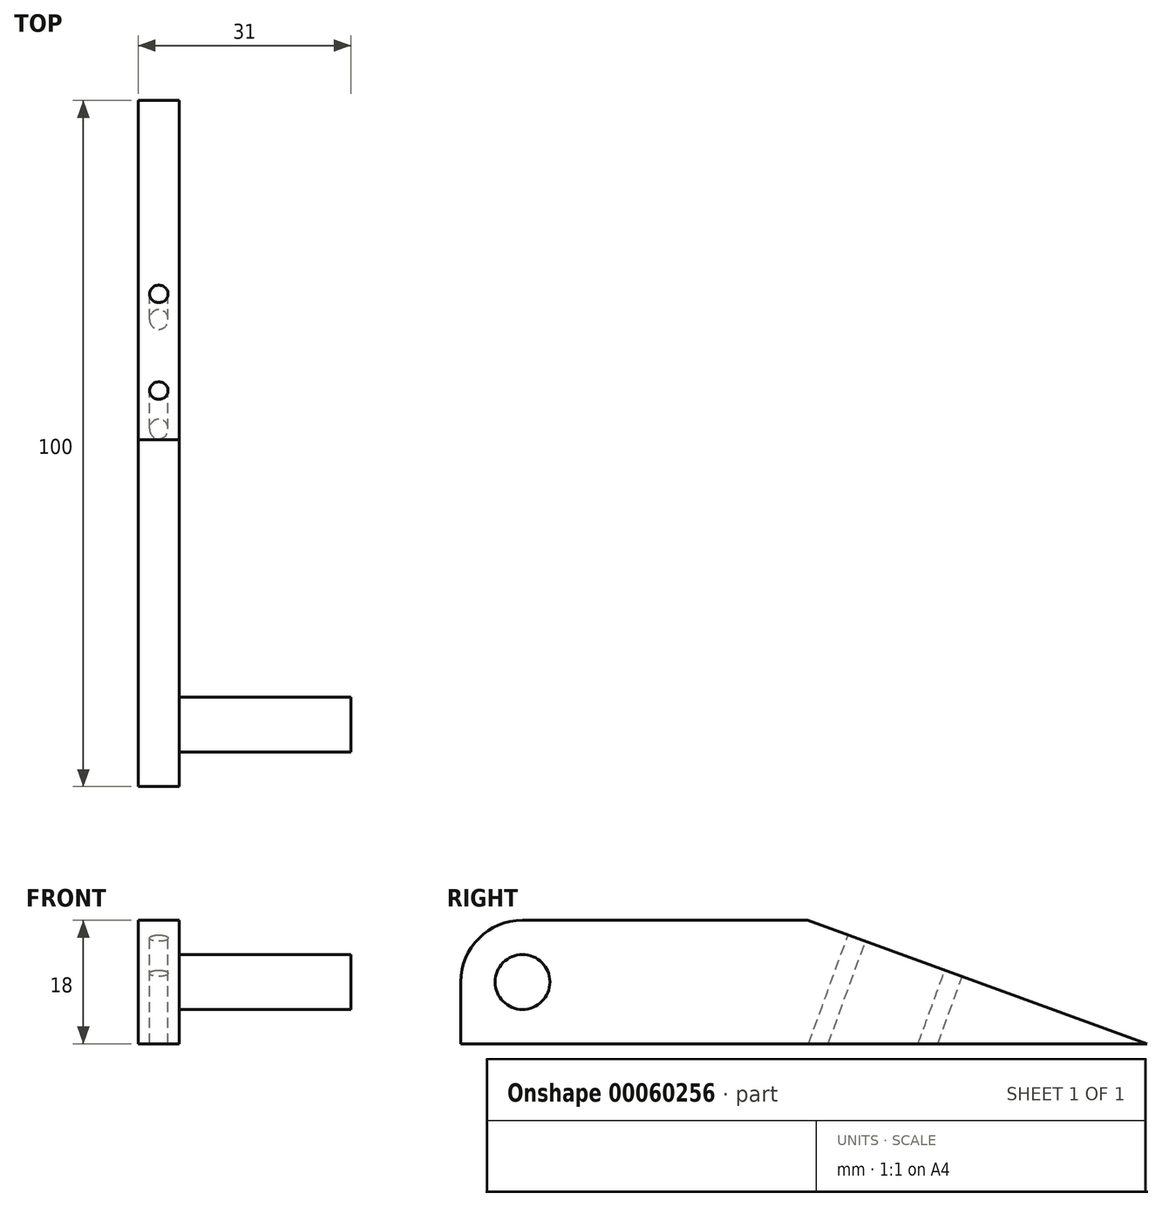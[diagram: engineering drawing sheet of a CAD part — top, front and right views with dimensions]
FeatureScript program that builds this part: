
annotation { "Feature Type Name" : "Feature", "Feature Type Description" : "" }
export const myFeature = defineFeature(function(context is Context, id is Id, definition is map)
    precondition{}
    {
        {
            var Q0;
            Q0=qCreatedBy(makeId("Right.planeOp"),FACE);
            var sketch = newSketch(context, id + "F0", { "sketchPlane" : qUnion([Q0])});
            skLineSegment(sketch, "E0", {"start": v(0, 0) * mm, "end": v(-49.45, 18) * mm});
            skLineSegment(sketch, "E1", {"start": v(-100, 0) * mm, "end": v(0, 0) * mm});
            skLineSegment(sketch, "E2", {"start": v(-49.45, 18) * mm, "end": v(-100, 18) * mm});
            skLineSegment(sketch, "E3", {"start": v(-100, 18) * mm, "end": v(-100, 0) * mm});
            skSolve(sketch);
        }
        {
            var Q0;
            Q0 = qSketchRegion(id + "F0", true);
            extrude(context, id + "F1", {"entities" : qUnion([Q0]), "depth" : 6 * mm});
        }
        {
            var Q0;
            Q0=makeQuery(id+"F1.opExtrude","SWEPT_EDGE",EDGE,{"disambiguationData":[OSD([sQuery(id+"F0.wireOp",EDGE,"E2"),sQuery(id+"F0.wireOp",EDGE,"E3")])]});
            fillet(context, id + "F2", {"entities" : qUnion([Q0]), "radius" : 9 * mm, "tangentPropagation" : true, "allowEdgeOverflow" : false});
        }
        {
            var Q0;
            Q0=makeQuery(id+"F1.opExtrude","CAP_FACE",FACE,{"disambiguationData":[OSD([sQuery(id+"F0.wireOp",EDGE,"E0"),sQuery(id+"F0.wireOp",EDGE,"E1"),sQuery(id+"F0.wireOp",EDGE,"E2"),sQuery(id+"F0.wireOp",EDGE,"E3")])],"isStart":false});
            var sketch = newSketch(context, id + "F3", { "sketchPlane" : qUnion([Q0])});
            skCircle(sketch, "E4", {"center": v(-91, 9) * mm, "radius": 4 * mm});
            skSolve(sketch);
        }
        {
            var Q0;
            Q0=makeQuery(id+"F3.imprint","IMPRINT",FACE,{"disambiguationData":[TD([[makeQuery(id+"F3.imprint","IMPRINT",EDGE,{"derivedFrom":sQuery(id+"F3.wireOp",EDGE,"E4")}),1.0]])]});
            extrude(context, id + "F4", {"entities" : qUnion([Q0]), "operationType" : NewBodyOperationType.ADD, "depth" : 25 * mm});
        }
        {
            var Q0;
            Q0=makeQuery(id+"F1.opExtrude","SWEPT_FACE",FACE,{"disambiguationData":[OSD([sQuery(id+"F0.wireOp",EDGE,"E0")])]});
            var sketch = newSketch(context, id + "F5", { "sketchPlane" : qUnion([Q0])});
            skCircle(sketch, "E5", {"center": v(3, -45) * mm, "radius": 1.35 * mm});
            skCircle(sketch, "E6", {"center": v(3, -30) * mm, "radius": 1.35 * mm});
            skLineSegment(sketch, "E7", {"start": v(3, -30) * mm, "end": v(6, -30) * mm, "construction": true});
            skLineSegment(sketch, "E8", {"start": v(6, -30) * mm, "end": v(3, -30) * mm, "construction": true});
            skLineSegment(sketch, "E9", {"start": v(3, -30) * mm, "end": v(0, -30) * mm, "construction": true});
            skSolve(sketch);
        }
        {
            var Q0;
            Q0 = qSketchRegion(id + "F5", true);
            extrude(context, id + "F6", {"entities" : qUnion([Q0]), "operationType" : NewBodyOperationType.REMOVE, "oppositeDirection" : true, "depth" : 25 * mm});
        }
    });
